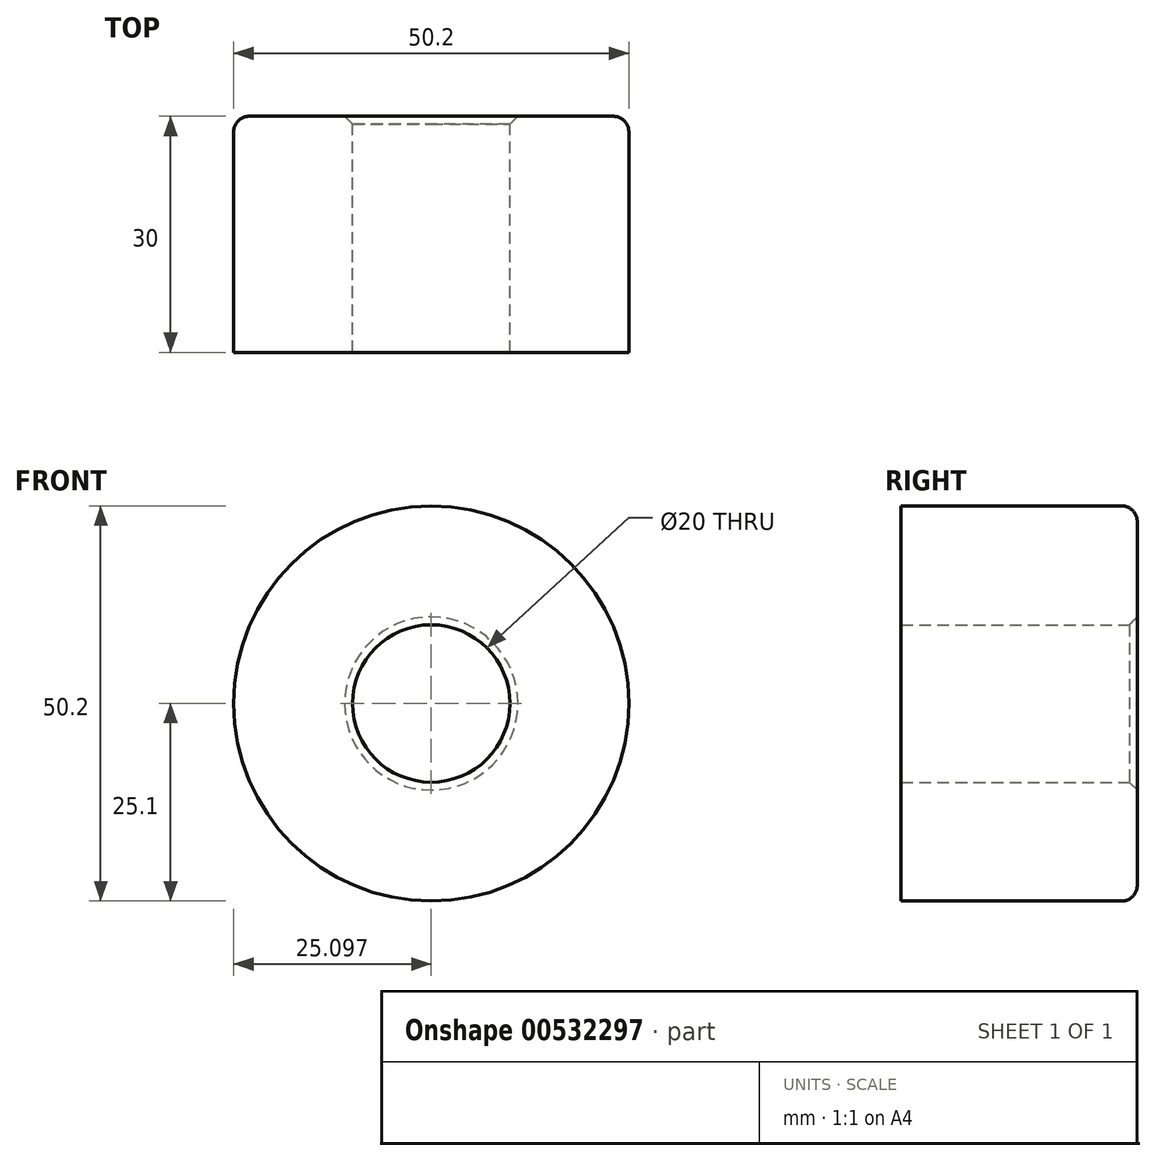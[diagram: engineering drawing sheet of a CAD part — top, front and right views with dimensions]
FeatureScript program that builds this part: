
annotation { "Feature Type Name" : "Feature", "Feature Type Description" : "" }
export const myFeature = defineFeature(function(context is Context, id is Id, definition is map)
    precondition{}
    {
        {
            var Q0;
            Q0=qCreatedBy(makeId("Front.planeOp"),FACE);
            var sketch = newSketch(context, id + "F0", { "sketchPlane" : qUnion([Q0])});
            skPoint(sketch, "E0", {"position": v(0, 0) * mm});
            skPoint(sketch, "E1", {"position": v(20.52, 0) * mm});
            skCircle(sketch, "E2", {"center": v(20.52, 0) * mm, "radius": 25.1 * mm});
            skSolve(sketch);
        }
        {
            var Q0;
            Q0=makeQuery(id+"F0.imprint","IMPRINT",FACE,{"disambiguationData":[TD([[makeQuery(id+"F0.imprint","IMPRINT",EDGE,{"derivedFrom":sQuery(id+"F0.wireOp",EDGE,"E2")}),1.0]])]});
            extrude(context, id + "F1", {"entities" : qUnion([Q0]), "depth" : 30 * mm, "offsetDistance" : 25 * mm});
        }
        {
            var Q0;
            Q0=makeQuery(id+"F1.opExtrude","CAP_EDGE",EDGE,{"disambiguationData":[OSD([sQuery(id+"F0.wireOp",EDGE,"E2")])],"isStart":true});
            fillet(context, id + "F2", {"entities" : qUnion([Q0]), "radius" : 2 * mm, "tangentPropagation" : true, "allowEdgeOverflow" : false});
        }
        {
            var Q0;
            Q0=makeQuery(id+"F1.opExtrude","CAP_FACE",FACE,{"disambiguationData":[OSD([sQuery(id+"F0.wireOp",EDGE,"E2")])],"isStart":false});
            var sketch = newSketch(context, id + "F3", { "sketchPlane" : qUnion([Q0])});
            skPoint(sketch, "E3", {"position": v(20.52, 0) * mm});
            skCircle(sketch, "E4", {"center": v(20.52, 0) * mm, "radius": 22.56 * mm});
            skSolve(sketch);
        }
        {
            var Q0;
            Q0=makeQuery(id+"F1.opExtrude","CAP_FACE",FACE,{"disambiguationData":[OSD([sQuery(id+"F0.wireOp",EDGE,"E2")])],"isStart":true});
            var sketch = newSketch(context, id + "F4", { "sketchPlane" : qUnion([Q0])});
            skPoint(sketch, "E5", {"position": v(-20.52, 0) * mm});
            skSolve(sketch);
        }
        {
            var Q0;
            Q0=sQuery(id+"F4.wireOp",VERTEX,"E5");
            var Q1;
            Q1=makeQuery(id+"F1.opExtrude","SWEPT_BODY",BODY,{"disambiguationData":[OSD([sQuery(id+"F0.wireOp",EDGE,"E2")])]});
            hole(context, id + "F5", {"style" : HoleStyle.C_SINK, "endStyle" : HoleEndStyle.BLIND, "holeDiameter" : 20 * mm, "cSinkDiameter" : 22 * mm, "cSinkAngle" : 90 * degree, "holeDepth" : 190 * mm, "isTappedThrough" : true, "tappedDepth" : 12 * mm, "tapClearance" : 3, "startFromSketch" : true, "locations" : qUnion([Q0]), "scope" : qUnion([Q1])});
        }
        {
            var Q0;
            Q0=qCreatedBy(makeId("Top.planeOp"),FACE);
            var sketch = newSketch(context, id + "F6", { "sketchPlane" : qUnion([Q0])});
            skPoint(sketch, "E6", {"position": v(19.41, -70) * mm});
            skPoint(sketch, "E7", {"position": v(19.41, -150) * mm});
            skLineSegment(sketch, "E8", {"start": v(41.91, -30) * mm, "end": v(41.91, -190) * mm});
            skLineSegment(sketch, "E9", {"start": v(-3.09, -190) * mm, "end": v(-3.09, -30) * mm});
            skLineSegment(sketch, "E10.0", {"start": v(41.91, -190) * mm, "end": v(-3.09, -190) * mm});
            skSolve(sketch);
        }
        {
            var Q0;
            Q0=sQuery(id+"F6.wireOp",VERTEX,"E6");
            var Q1;
            Q1=sQuery(id+"F6.wireOp",VERTEX,"E7");
            var Q2;
            Q2=makeQuery(id+"F1.opExtrude","SWEPT_BODY",BODY,{"disambiguationData":[OSD([sQuery(id+"F0.wireOp",EDGE,"E2")])]});
            hole(context, id + "F7", {"style" : HoleStyle.SIMPLE, "endStyle" : HoleEndStyle.THROUGH, "oppositeDirection" : true, "holeDiameter" : 4 * mm, "isTappedThrough" : true, "tappedDepth" : 12 * mm, "tapClearance" : 3, "startFromSketch" : true, "locations" : qUnion([Q0, Q1]), "scope" : qUnion([Q2])});
        }
        {
            var Q0;
            Q0=qCreatedBy(makeId("Top.planeOp"),FACE);
            var sketch = newSketch(context, id + "F8", { "sketchPlane" : qUnion([Q0])});
            skPoint(sketch, "E11", {"position": v(20.57, -70) * mm});
            skPoint(sketch, "E12", {"position": v(18.68, -70) * mm});
            skSolve(sketch);
        }
        {
            var Q0;
            Q0=sQuery(id+"F8.wireOp",VERTEX,"E11");
            var Q1;
            Q1=makeQuery(id+"F1.opExtrude","SWEPT_BODY",BODY,{"disambiguationData":[OSD([sQuery(id+"F0.wireOp",EDGE,"E2")])]});
            hole(context, id + "F9", {"style" : HoleStyle.SIMPLE, "endStyle" : HoleEndStyle.THROUGH, "holeDiameter" : 4 * mm, "isTappedThrough" : true, "tappedDepth" : 12 * mm, "tapClearance" : 3, "startFromSketch" : true, "locations" : qUnion([Q0]), "scope" : qUnion([Q1])});
        }
    });
